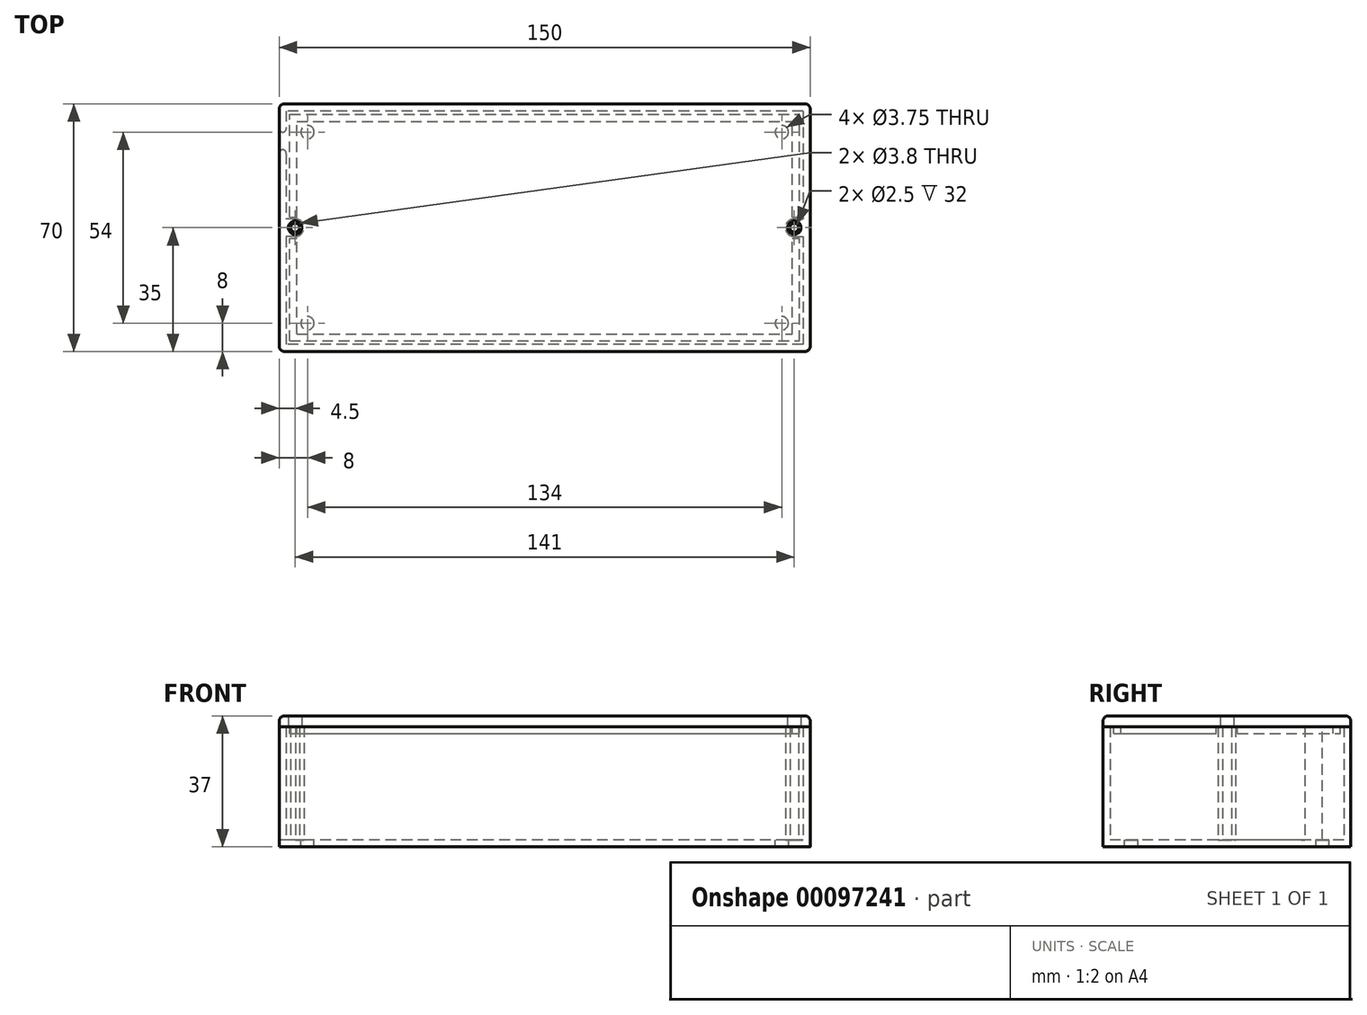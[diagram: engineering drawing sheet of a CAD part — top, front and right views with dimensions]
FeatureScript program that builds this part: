
annotation { "Feature Type Name" : "Feature", "Feature Type Description" : "" }
export const myFeature = defineFeature(function(context is Context, id is Id, definition is map)
    precondition{}
    {
        {
            var Q0;
            Q0=qCreatedBy(makeId("Top.planeOp"),FACE);
            var sketch = newSketch(context, id + "F0", { "sketchPlane" : qUnion([Q0])});
            skLineSegment(sketch, "E0.bottom", {"start": v(75, 35) * mm, "end": v(-75, 35) * mm});
            skLineSegment(sketch, "E0.top", {"start": v(75, -35) * mm, "end": v(-75, -35) * mm});
            skLineSegment(sketch, "E0.left", {"start": v(75, 35) * mm, "end": v(75, -35) * mm});
            skLineSegment(sketch, "E0.right", {"start": v(-75, 35) * mm, "end": v(-75, -35) * mm});
            skPoint(sketch, "E0.middle", {"position": v(0, 0) * mm});
            skCircle(sketch, "E1", {"center": v(-67, 27) * mm, "radius": 1.88 * mm});
            skCircle(sketch, "E2", {"center": v(-67, -27) * mm, "radius": 1.88 * mm});
            skCircle(sketch, "E3", {"center": v(67, -27) * mm, "radius": 1.88 * mm});
            skCircle(sketch, "E4", {"center": v(67, 27) * mm, "radius": 1.88 * mm});
            skSolve(sketch);
        }
        {
            var Q0;
            Q0=makeQuery(id+"F0.imprint","IMPRINT",FACE,{"disambiguationData":[TD([[makeQuery(id+"F0.imprint","IMPRINT",EDGE,{"derivedFrom":sQuery(id+"F0.wireOp",EDGE,"E0.bottom")}),1.0]])]});
            extrude(context, id + "F1", {"entities" : qUnion([Q0]), "oppositeDirection" : true, "depth" : 2 * mm});
        }
        {
            var Q0;
            Q0=qCreatedBy(makeId("Top.planeOp"),FACE);
            var sketch = newSketch(context, id + "F2", { "sketchPlane" : qUnion([Q0])});
            skLineSegment(sketch, "E5.bottom", {"start": v(75, 35) * mm, "end": v(-75, 35) * mm});
            skLineSegment(sketch, "E5.top", {"start": v(75, -35) * mm, "end": v(-75, -35) * mm});
            skLineSegment(sketch, "E5.left", {"start": v(75, 35) * mm, "end": v(75, -35) * mm});
            skLineSegment(sketch, "E5.right", {"start": v(-75, 35) * mm, "end": v(-75, -35) * mm});
            skPoint(sketch, "E5.middle", {"position": v(0, 0) * mm});
            skLineSegment(sketch, "E6.bottom", {"start": v(73, 33) * mm, "end": v(-73, 33) * mm});
            skLineSegment(sketch, "E6.top", {"start": v(73, -33) * mm, "end": v(-73, -33) * mm});
            skLineSegment(sketch, "E6.left", {"start": v(73, 33) * mm, "end": v(73, 2.45) * mm});
            skLineSegment(sketch, "E6.right", {"start": v(-73, 33) * mm, "end": v(-73, 2.5) * mm});
            skLineSegment(sketch, "E7.bottom", {"start": v(-75, 27) * mm, "end": v(-73, 27) * mm});
            skLineSegment(sketch, "E7.top", {"start": v(-75, 22) * mm, "end": v(-73, 22) * mm});
            skLineSegment(sketch, "E7.left", {"start": v(-75, 27) * mm, "end": v(-75, 22) * mm});
            skLineSegment(sketch, "E7.right", {"start": v(-73, 27) * mm, "end": v(-73, 22) * mm});
            skArc(sketch, "E8", {"start": v(-70.57, -2.5) * mm, "mid": v(-68, 0.04) * mm, "end": v(-70.65, 2.5) * mm});
            skPoint(sketch, "E8.centerSnap0", {"position": v(-73, 0) * mm});
            skArc(sketch, "E9", {"start": v(70.55, 2.5) * mm, "mid": v(68, 0.02) * mm, "end": v(70.51, -2.5) * mm});
            skPoint(sketch, "E9.centerSnap0", {"position": v(73, 0) * mm});
            skCircle(sketch, "E10", {"center": v(-70.5, 0) * mm, "radius": 1.25 * mm});
            skCircle(sketch, "E11", {"center": v(70.5, 0) * mm, "radius": 1.25 * mm});
            skLineSegment(sketch, "E12", {"start": v(-70.35, 2.5) * mm, "end": v(-73, 2.5) * mm});
            skLineSegment(sketch, "E13", {"start": v(-70.43, -2.5) * mm, "end": v(-73, -2.5) * mm});
            skLineSegment(sketch, "E14", {"start": v(70.55, 2.5) * mm, "end": v(73, 2.45) * mm});
            skLineSegment(sketch, "E15", {"start": v(70.51, -2.5) * mm, "end": v(73, -2.5) * mm});
            skLineSegment(sketch, "E16.trimOffspring", {"start": v(-73, -2.5) * mm, "end": v(-73, -33) * mm});
            skLineSegment(sketch, "E17.trimOffspring", {"start": v(73, -2.5) * mm, "end": v(73, -33) * mm});
            skSolve(sketch);
        }
        {
            var Q0;
            {var subQ12=sQuery(id+"F2.wireOp",EDGE,"E5.bottom");Q0=makeQuery(id+"F2.imprint","IMPRINT",FACE,{"disambiguationData":[TD([[makeQuery(id+"F2.imprint","IMPRINT",EDGE,{"derivedFrom":subQ12}),1.0]])]});}
            extrude(context, id + "F3", {"entities" : qUnion([Q0]), "operationType" : NewBodyOperationType.ADD, "depth" : 32 * mm});
        }
        {
            var Q0;
            Q0=makeQuery(id+"F3.opExtrude","CAP_FACE",FACE,{"disambiguationData":[OSD([sQuery(id+"F2.wireOp",EDGE,"E5.bottom"),sQuery(id+"F2.wireOp",EDGE,"E5.top"),sQuery(id+"F2.wireOp",EDGE,"E5.left"),sQuery(id+"F2.wireOp",EDGE,"E5.right"),sQuery(id+"F2.wireOp",EDGE,"E6.bottom"),sQuery(id+"F2.wireOp",EDGE,"E6.top"),sQuery(id+"F2.wireOp",EDGE,"E6.left"),sQuery(id+"F2.wireOp",EDGE,"E6.right"),sQuery(id+"F2.wireOp",EDGE,"E7.bottom"),sQuery(id+"F2.wireOp",EDGE,"E7.top"),sQuery(id+"F2.wireOp",EDGE,"E8"),sQuery(id+"F2.wireOp",EDGE,"E9"),sQuery(id+"F2.wireOp",EDGE,"E10"),sQuery(id+"F2.wireOp",EDGE,"E11"),sQuery(id+"F2.wireOp",EDGE,"E12"),sQuery(id+"F2.wireOp",EDGE,"E13"),sQuery(id+"F2.wireOp",EDGE,"E14"),sQuery(id+"F2.wireOp",EDGE,"E15"),sQuery(id+"F2.wireOp",EDGE,"E16.trimOffspring"),sQuery(id+"F2.wireOp",EDGE,"E17.trimOffspring")])],"isStart":false});
            var sketch = newSketch(context, id + "F4", { "sketchPlane" : qUnion([Q0])});
            skLineSegment(sketch, "E18.bottom", {"start": v(75, 35) * mm, "end": v(-75, 35) * mm});
            skLineSegment(sketch, "E18.top", {"start": v(75, -35) * mm, "end": v(-75, -35) * mm});
            skLineSegment(sketch, "E18.left", {"start": v(75, 35) * mm, "end": v(75, -35) * mm});
            skLineSegment(sketch, "E18.right", {"start": v(-75, 35) * mm, "end": v(-75, -35) * mm});
            skPoint(sketch, "E18.middle", {"position": v(0, 0) * mm});
            skCircle(sketch, "E19", {"center": v(-70.5, 0) * mm, "radius": 1.9 * mm});
            skCircle(sketch, "E20", {"center": v(70.5, 0) * mm, "radius": 1.9 * mm});
            skSolve(sketch);
        }
        {
            var Q0;
            Q0 = qSketchRegion(id + "F4", true);
            extrude(context, id + "F5", {"entities" : qUnion([Q0]), "depth" : 3 * mm});
        }
        {
            var Q0;
            {var subQ5=sQuery(id+"F2.wireOp",EDGE,"E6.bottom");Q0=makeQuery(id+"F4.imprint","IMPRINT",FACE,{"disambiguationData":[TD([[makeQuery(id+"F4.imprint","IMPRINT",EDGE,{"derivedFrom":makeQuery(id+"F3.opExtrude","CAP_EDGE",EDGE,{"disambiguationData":[OSD([subQ5])],"isStart":false})}),1.0]])]});}
            var sketch = newSketch(context, id + "F6", { "sketchPlane" : qUnion([Q0])});
            skLineSegment(sketch, "E21.bottom", {"start": v(-72, -32) * mm, "end": v(72, -32) * mm});
            skLineSegment(sketch, "E21.top", {"start": v(-72, 32) * mm, "end": v(72, 32) * mm});
            skLineSegment(sketch, "E21.left", {"start": v(-72, -32) * mm, "end": v(-72, -3) * mm});
            skLineSegment(sketch, "E21.right", {"start": v(72, -32) * mm, "end": v(72, -2.96) * mm});
            skPoint(sketch, "E21.middle", {"position": v(0, 0) * mm});
            skLineSegment(sketch, "E22.bottom", {"start": v(-70, -30) * mm, "end": v(70, -30) * mm});
            skLineSegment(sketch, "E22.top", {"start": v(-70, 30) * mm, "end": v(70, 30) * mm});
            skLineSegment(sketch, "E22.left", {"start": v(-70, -30) * mm, "end": v(-70, -3) * mm});
            skLineSegment(sketch, "E22.right", {"start": v(70, -30) * mm, "end": v(70, -2.96) * mm});
            skLineSegment(sketch, "E23.bottom", {"start": v(-72, -3) * mm, "end": v(-70, -3) * mm});
            skLineSegment(sketch, "E23.top", {"start": v(-72, 2.96) * mm, "end": v(-70, 2.96) * mm});
            skLineSegment(sketch, "E24.bottom", {"start": v(70, -2.96) * mm, "end": v(72, -2.96) * mm});
            skLineSegment(sketch, "E24.top", {"start": v(70, 2.96) * mm, "end": v(72, 2.96) * mm});
            skLineSegment(sketch, "E25.trimOffspring", {"start": v(-72, 2.96) * mm, "end": v(-72, 32) * mm});
            skLineSegment(sketch, "E26.trimOffspring", {"start": v(-70, 2.96) * mm, "end": v(-70, 30) * mm});
            skLineSegment(sketch, "E27.trimOffspring", {"start": v(70, 2.96) * mm, "end": v(70, 30) * mm});
            skLineSegment(sketch, "E28.trimOffspring", {"start": v(72, 2.96) * mm, "end": v(72, 32) * mm});
            skSolve(sketch);
        }
        {
            var Q0;
            Q0=makeQuery(id+"F6.imprint","IMPRINT",FACE,{"disambiguationData":[TD([[makeQuery(id+"F6.imprint","IMPRINT",EDGE,{"derivedFrom":sQuery(id+"F6.wireOp",EDGE,"E21.bottom")}),1.0]])]});
            var Q1;
            Q1=makeQuery(id+"F6.imprint","IMPRINT",FACE,{"disambiguationData":[TD([[makeQuery(id+"F6.imprint","IMPRINT",EDGE,{"derivedFrom":sQuery(id+"F6.wireOp",EDGE,"E21.top")}),-1.0]])]});
            extrude(context, id + "F7", {"entities" : qUnion([Q0, Q1]), "operationType" : NewBodyOperationType.ADD, "oppositeDirection" : true, "depth" : 2 * mm});
        }
        {
            var Q0;
            Q0=makeQuery(id+"F3.boolean.opBoolean","MERGE",EDGE,{"derivedFrom":[makeQuery(id+"F1.opExtrude","SWEPT_EDGE",EDGE,{"disambiguationData":[OSD([sQuery(id+"F0.wireOp",EDGE,"E0.top"),sQuery(id+"F0.wireOp",EDGE,"E0.right")])]}),makeQuery(id+"F3.opExtrude","SWEPT_EDGE",EDGE,{"disambiguationData":[OSD([sQuery(id+"F2.wireOp",EDGE,"E5.top"),sQuery(id+"F2.wireOp",EDGE,"E5.right")])]})]});
            var Q1;
            Q1=makeQuery(id+"F3.boolean.opBoolean","MERGE",EDGE,{"derivedFrom":[makeQuery(id+"F1.opExtrude","SWEPT_EDGE",EDGE,{"disambiguationData":[OSD([sQuery(id+"F0.wireOp",EDGE,"E0.top"),sQuery(id+"F0.wireOp",EDGE,"E0.left")])]}),makeQuery(id+"F3.opExtrude","SWEPT_EDGE",EDGE,{"disambiguationData":[OSD([sQuery(id+"F2.wireOp",EDGE,"E5.top"),sQuery(id+"F2.wireOp",EDGE,"E5.left")])]})]});
            var Q2;
            Q2=makeQuery(id+"F3.boolean.opBoolean","MERGE",EDGE,{"derivedFrom":[makeQuery(id+"F1.opExtrude","SWEPT_EDGE",EDGE,{"disambiguationData":[OSD([sQuery(id+"F0.wireOp",EDGE,"E0.bottom"),sQuery(id+"F0.wireOp",EDGE,"E0.left")])]}),makeQuery(id+"F3.opExtrude","SWEPT_EDGE",EDGE,{"disambiguationData":[OSD([sQuery(id+"F2.wireOp",EDGE,"E5.bottom"),sQuery(id+"F2.wireOp",EDGE,"E5.left")])]})]});
            var Q3;
            Q3=makeQuery(id+"F3.boolean.opBoolean","MERGE",EDGE,{"derivedFrom":[makeQuery(id+"F1.opExtrude","SWEPT_EDGE",EDGE,{"disambiguationData":[OSD([sQuery(id+"F0.wireOp",EDGE,"E0.bottom"),sQuery(id+"F0.wireOp",EDGE,"E0.right")])]}),makeQuery(id+"F3.opExtrude","SWEPT_EDGE",EDGE,{"disambiguationData":[OSD([sQuery(id+"F2.wireOp",EDGE,"E5.bottom"),sQuery(id+"F2.wireOp",EDGE,"E5.right")])]})]});
            var Q4;
            Q4=makeQuery(id+"F5.opExtrude","SWEPT_EDGE",EDGE,{"disambiguationData":[OSD([sQuery(id+"F4.wireOp",EDGE,"E18.top"),sQuery(id+"F4.wireOp",EDGE,"E18.right")])]});
            var Q5;
            Q5=makeQuery(id+"F5.opExtrude","SWEPT_EDGE",EDGE,{"disambiguationData":[OSD([sQuery(id+"F4.wireOp",EDGE,"E18.bottom"),sQuery(id+"F4.wireOp",EDGE,"E18.right")])]});
            var Q6;
            Q6=makeQuery(id+"F5.opExtrude","SWEPT_EDGE",EDGE,{"disambiguationData":[OSD([sQuery(id+"F4.wireOp",EDGE,"E18.bottom"),sQuery(id+"F4.wireOp",EDGE,"E18.left")])]});
            var Q7;
            Q7=makeQuery(id+"F5.opExtrude","SWEPT_EDGE",EDGE,{"disambiguationData":[OSD([sQuery(id+"F4.wireOp",EDGE,"E18.top"),sQuery(id+"F4.wireOp",EDGE,"E18.left")])]});
            var Q8;
            Q8=makeQuery(id+"F5.opExtrude","CAP_EDGE",EDGE,{"disambiguationData":[OSD([sQuery(id+"F4.wireOp",EDGE,"E18.right")])],"isStart":false});
            var Q9;
            Q9=makeQuery(id+"F5.opExtrude","CAP_EDGE",EDGE,{"disambiguationData":[OSD([sQuery(id+"F4.wireOp",EDGE,"E18.bottom")])],"isStart":false});
            var Q10;
            Q10=makeQuery(id+"F5.opExtrude","CAP_EDGE",EDGE,{"disambiguationData":[OSD([sQuery(id+"F4.wireOp",EDGE,"E18.left")])],"isStart":false});
            var Q11;
            Q11=makeQuery(id+"F5.opExtrude","CAP_EDGE",EDGE,{"disambiguationData":[OSD([sQuery(id+"F4.wireOp",EDGE,"E18.top")])],"isStart":false});
            fillet(context, id + "F8", {"entities" : qUnion([Q0, Q1, Q2, Q3, Q4, Q5, Q6, Q7, Q8, Q9, Q10, Q11]), "radius" : 1.5 * mm, "tangentPropagation" : true, "allowEdgeOverflow" : false});
        }
        {
            var Q0;
            Q0=makeQuery(id+"F3.opExtrude","SWEPT_EDGE",EDGE,{"disambiguationData":[OSD([sQuery(id+"F2.wireOp",EDGE,"E5.right"),sQuery(id+"F2.wireOp",EDGE,"E7.top"),sQuery(id+"F2.wireOp",EDGE,"E7.left")])]});
            var Q1;
            Q1=makeQuery(id+"F3.opExtrude","SWEPT_EDGE",EDGE,{"disambiguationData":[OSD([sQuery(id+"F2.wireOp",EDGE,"E6.right"),sQuery(id+"F2.wireOp",EDGE,"E7.top"),sQuery(id+"F2.wireOp",EDGE,"E7.right")])]});
            var Q2;
            Q2=makeQuery(id+"F3.opExtrude","SWEPT_EDGE",EDGE,{"disambiguationData":[OSD([sQuery(id+"F2.wireOp",EDGE,"E5.right"),sQuery(id+"F2.wireOp",EDGE,"E7.bottom"),sQuery(id+"F2.wireOp",EDGE,"E7.left")])]});
            var Q3;
            Q3=makeQuery(id+"F3.opExtrude","SWEPT_EDGE",EDGE,{"disambiguationData":[OSD([sQuery(id+"F2.wireOp",EDGE,"E6.right"),sQuery(id+"F2.wireOp",EDGE,"E7.bottom"),sQuery(id+"F2.wireOp",EDGE,"E7.right")])]});
            fillet(context, id + "F9", {"entities" : qUnion([Q0, Q1, Q2, Q3]), "radius" : 1 * mm, "tangentPropagation" : true, "allowEdgeOverflow" : false});
        }
    });
